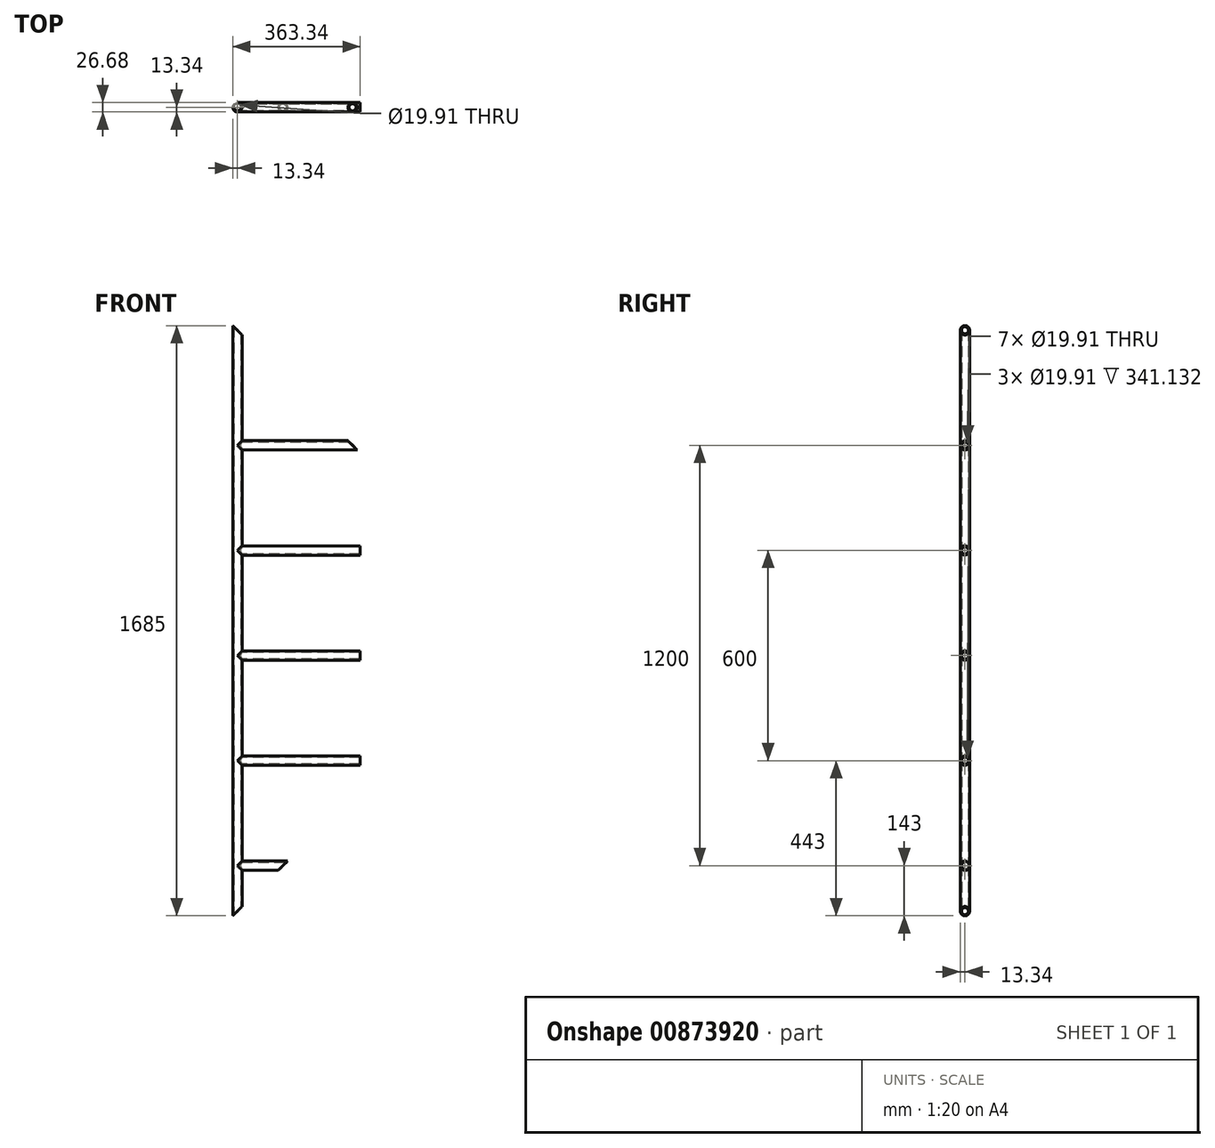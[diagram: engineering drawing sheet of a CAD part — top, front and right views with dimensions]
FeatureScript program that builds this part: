
annotation { "Feature Type Name" : "Feature", "Feature Type Description" : "" }
export const myFeature = defineFeature(function(context is Context, id is Id, definition is map)
    precondition{}
    {
        {
            var Q0;
            Q0=qCreatedBy(makeId("Front.planeOp"),FACE);
            var sketch = newSketch(context, id + "F0", { "sketchPlane" : qUnion([Q0])});
            skLineSegment(sketch, "E0", {"start": v(0, 842.5) * mm, "end": v(0, -842.5) * mm});
            skLineSegment(sketch, "E1", {"start": v(0, -699.5) * mm, "end": v(145, -699.5) * mm});
            skLineSegment(sketch, "E2", {"start": v(0, -99.5) * mm, "end": v(335, -99.5) * mm});
            skLineSegment(sketch, "E3", {"start": v(0, 500.5) * mm, "end": v(345, 500.5) * mm});
            skLineSegment(sketch, "E4", {"start": v(0, 200.5) * mm, "end": v(335, 200.5) * mm});
            skLineSegment(sketch, "E5", {"start": v(0, -399.5) * mm, "end": v(335, -399.5) * mm});
            skLineSegment(sketch, "E6", {"start": v(-13.33, -842.5) * mm, "end": v(13.33, -842.5) * mm, "construction": true});
            skLineSegment(sketch, "E7", {"start": v(-13.34, 842.5) * mm, "end": v(13.34, 842.5) * mm, "construction": true});
            skLineSegment(sketch, "E8", {"start": v(-13.33, -842.5) * mm, "end": v(829.16, 0) * mm});
            skLineSegment(sketch, "E9", {"start": v(-13.33, 842.5) * mm, "end": v(829.16, 0) * mm});
            skLineSegment(sketch, "E10", {"start": v(-13.34, 842.5) * mm, "end": v(1131.41, 842.5) * mm});
            skLineSegment(sketch, "E11", {"start": v(1131.41, 842.5) * mm, "end": v(1131.41, -842.5) * mm});
            skLineSegment(sketch, "E12", {"start": v(-13.33, -842.5) * mm, "end": v(1131.41, -842.5) * mm});
            skSolve(sketch);
        }
        {
            var Q0;
            Q0=qCreatedBy(makeId("Top.planeOp"),FACE);
            var sketch = newSketch(context, id + "F1", { "sketchPlane" : qUnion([Q0])});
            skCircle(sketch, "E13", {"center": v(0, 0) * mm, "radius": 13.34 * mm});
            skCircle(sketch, "E14.0", {"center": v(0, 0) * mm, "radius": 9.96 * mm});
            skSolve(sketch);
        }
        {
            var Q0;
            Q0=qCreatedBy(makeId("Right.planeOp"),FACE);
            var sketch = newSketch(context, id + "F2", { "sketchPlane" : qUnion([Q0])});
            skCircle(sketch, "E15", {"center": v(0, -699.5) * mm, "radius": 13.34 * mm});
            skCircle(sketch, "E16.0", {"center": v(0, -699.5) * mm, "radius": 9.96 * mm});
            skCircle(sketch, "E17.0.1.0", {"center": v(0, -399.5) * mm, "radius": 13.34 * mm});
            skCircle(sketch, "E17.0.1.1", {"center": v(0, -399.5) * mm, "radius": 9.96 * mm});
            skCircle(sketch, "E17.0.2.0", {"center": v(0, -99.5) * mm, "radius": 13.34 * mm});
            skCircle(sketch, "E17.0.2.1", {"center": v(0, -99.5) * mm, "radius": 9.96 * mm});
            skCircle(sketch, "E17.0.3.0", {"center": v(0, 200.5) * mm, "radius": 13.34 * mm});
            skCircle(sketch, "E17.0.3.1", {"center": v(0, 200.5) * mm, "radius": 9.96 * mm});
            skCircle(sketch, "E17.0.4.0", {"center": v(0, 500.5) * mm, "radius": 13.34 * mm});
            skCircle(sketch, "E17.0.4.1", {"center": v(0, 500.5) * mm, "radius": 9.96 * mm});
            skLineSegment(sketch, "E17.direction1", {"start": v(0, -699.5) * mm, "end": v(25, -699.5) * mm, "construction": true});
            skLineSegment(sketch, "E17.direction2", {"start": v(0, -699.5) * mm, "end": v(0, -399.5) * mm, "construction": true});
            skSolve(sketch);
        }
        {
            var Q0;
            Q0=makeQuery(id+"F2.imprint","IMPRINT",FACE,{"disambiguationData":[TD([[makeQuery(id+"F2.imprint","IMPRINT",EDGE,{"derivedFrom":sQuery(id+"F2.wireOp",EDGE,"E15")}),1.0]])]});
            var Q1;
            Q1=sQuery(id+"F0.wireOp",EDGE,"E1");
            sweep(context, id + "F3", {"profiles" : qUnion([Q0]), "path" : qUnion([Q1])});
        }
        {
            var Q0;
            Q0=makeQuery(id+"F2.imprint","IMPRINT",FACE,{"disambiguationData":[TD([[makeQuery(id+"F2.imprint","IMPRINT",EDGE,{"derivedFrom":sQuery(id+"F2.wireOp",EDGE,"E17.0.4.0")}),1.0]])]});
            var Q1;
            Q1=sQuery(id+"F0.wireOp",EDGE,"E3");
            sweep(context, id + "F4", {"profiles" : qUnion([Q0]), "path" : qUnion([Q1])});
        }
        {
            var Q0;
            Q0=makeQuery(id+"F2.imprint","IMPRINT",FACE,{"disambiguationData":[TD([[makeQuery(id+"F2.imprint","IMPRINT",EDGE,{"derivedFrom":sQuery(id+"F2.wireOp",EDGE,"E17.0.3.0")}),1.0]])]});
            var Q1;
            Q1=makeQuery(id+"F2.imprint","IMPRINT",FACE,{"disambiguationData":[TD([[makeQuery(id+"F2.imprint","IMPRINT",EDGE,{"derivedFrom":sQuery(id+"F2.wireOp",EDGE,"E17.0.2.0")}),1.0]])]});
            var Q2;
            Q2=makeQuery(id+"F2.imprint","IMPRINT",FACE,{"disambiguationData":[TD([[makeQuery(id+"F2.imprint","IMPRINT",EDGE,{"derivedFrom":sQuery(id+"F2.wireOp",EDGE,"E17.0.1.0")}),1.0]])]});
            extrude(context, id + "F5", {"entities" : qUnion([Q0, Q1, Q2]), "depth" : 350 * mm, "offsetDistance" : 25 * mm});
        }
        {
            var Q0;
            Q0=makeQuery(id+"F1.imprint","IMPRINT",FACE,{"disambiguationData":[TD([[makeQuery(id+"F1.imprint","IMPRINT",EDGE,{"derivedFrom":sQuery(id+"F1.wireOp",EDGE,"E13")}),1.0]])]});
            var Q1;
            Q1=makeQuery(id+"F1.imprint","IMPRINT",FACE,{"disambiguationData":[TD([[makeQuery(id+"F1.imprint","IMPRINT",EDGE,{"derivedFrom":sQuery(id+"F1.wireOp",EDGE,"E14.0")}),1.0]])]});
            extrude(context, id + "F6", {"entities" : qUnion([Q0, Q1]), "operationType" : NewBodyOperationType.REMOVE, "oppositeDirection" : true, "depth" : 1800 * mm, "offsetDistance" : 25 * mm, "symmetric" : true});
        }
        {
            var Q0;
            Q0=makeQuery(id+"F1.imprint","IMPRINT",FACE,{"disambiguationData":[TD([[makeQuery(id+"F1.imprint","IMPRINT",EDGE,{"derivedFrom":sQuery(id+"F1.wireOp",EDGE,"E13")}),1.0]])]});
            extrude(context, id + "F7", {"entities" : qUnion([Q0]), "depth" : 1685 * mm, "offsetDistance" : 25 * mm, "symmetric" : true});
        }
        {
            var Q0;
            Q0=makeQuery(id+"F2.imprint","IMPRINT",FACE,{"disambiguationData":[TD([[makeQuery(id+"F2.imprint","IMPRINT",EDGE,{"derivedFrom":sQuery(id+"F2.wireOp",EDGE,"E17.0.4.1")}),1.0]])]});
            var Q1;
            Q1=makeQuery(id+"F2.imprint","IMPRINT",FACE,{"disambiguationData":[TD([[makeQuery(id+"F2.imprint","IMPRINT",EDGE,{"derivedFrom":sQuery(id+"F2.wireOp",EDGE,"E17.0.3.1")}),1.0]])]});
            var Q2;
            Q2=makeQuery(id+"F2.imprint","IMPRINT",FACE,{"disambiguationData":[TD([[makeQuery(id+"F2.imprint","IMPRINT",EDGE,{"derivedFrom":sQuery(id+"F2.wireOp",EDGE,"E17.0.2.1")}),1.0]])]});
            var Q3;
            Q3=makeQuery(id+"F2.imprint","IMPRINT",FACE,{"disambiguationData":[TD([[makeQuery(id+"F2.imprint","IMPRINT",EDGE,{"derivedFrom":sQuery(id+"F2.wireOp",EDGE,"E17.0.1.1")}),1.0]])]});
            var Q4;
            Q4=makeQuery(id+"F2.imprint","IMPRINT",FACE,{"disambiguationData":[TD([[makeQuery(id+"F2.imprint","IMPRINT",EDGE,{"derivedFrom":sQuery(id+"F2.wireOp",EDGE,"E16.0")}),1.0]])]});
            extrude(context, id + "F8", {"entities" : qUnion([Q0, Q1, Q2, Q3, Q4]), "operationType" : NewBodyOperationType.REMOVE, "depth" : 25 * mm, "offsetDistance" : 25 * mm});
        }
        {
            var Q0;
            {var subQ11=sQuery(id+"F0.wireOp",EDGE,"E11");Q0=makeQuery(id+"F0.imprint","IMPRINT",FACE,{"disambiguationData":[TD([[makeQuery(id+"F0.imprint","IMPRINT",EDGE,{"derivedFrom":subQ11}),-1.0]])]});}
            var Q1;
            {var subQ0=sQuery(id+"F0.wireOp",EDGE,"E12");var subQ1=sQuery(id+"F0.wireOp",EDGE,"E0");var subQ2=makeQuery(id+"F0.imprint","INTERSECT",VERTEX,{"derivedFrom":[subQ1,subQ0]});Q1=makeQuery(id+"F0.imprint","IMPRINT",FACE,{"disambiguationData":[TD([[makeQuery(id+"F0.imprint","IMPRINT",EDGE,{"disambiguationData":[TD([[subQ2,1.0]])],"derivedFrom":subQ1}),-1.0]])]});}
            var Q2;
            {var subQ0=sQuery(id+"F0.wireOp",EDGE,"E10");var subQ1=sQuery(id+"F0.wireOp",EDGE,"E0");var subQ2=makeQuery(id+"F0.imprint","INTERSECT",VERTEX,{"derivedFrom":[subQ1,subQ0]});Q2=makeQuery(id+"F0.imprint","IMPRINT",FACE,{"disambiguationData":[TD([[makeQuery(id+"F0.imprint","IMPRINT",EDGE,{"disambiguationData":[TD([[subQ2,-1.0]])],"derivedFrom":subQ1}),-1.0]])]});}
            extrude(context, id + "F9", {"entities" : qUnion([Q0, Q1, Q2]), "operationType" : NewBodyOperationType.REMOVE, "oppositeDirection" : true, "depth" : 50 * mm, "offsetDistance" : 25 * mm, "symmetric" : true});
        }
    });
